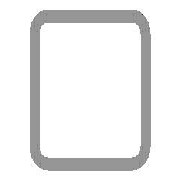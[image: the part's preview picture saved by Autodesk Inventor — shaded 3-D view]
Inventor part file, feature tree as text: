
AUTODESK INVENTOR PART (.ipt)
format: ipt  version: 2024.3 (Build 283343000, 343)  size: 143,360 bytes
history: native  units: mm (DEFAULTED — no unit token found)
features: other x4, plane x2, split x1, sketch x1
ambient origin geometry x8: Origin, YZ Plane, XZ Plane, XY Plane, X Axis, Y Axis, Z Axis, Center Point
bodies: Solid1 (feature_tree), Body (feature_tree)
feature tree (8):
  parser-record x1  (decoder bookkeeping rows leaked as tree rows — omitted from the tree; the rows remain in map.json)
  other  "Driven Length"
  other  "Start Plane"
  other  "End Plane"
  plane  "Work Plane4"
  split  "Split1"
  sketch  "Sketch3"  dims[d3=254.989146mm d4=0.0mm d7=6.0mm d9=100.0mm d11=100.0mm d12=3.0mm d13=-0.0mm d14=254.989146mm d15=50.0mm d16=50.0mm d17=90.0deg d18=254.989146mm]
  plane  "Work Plane3"
